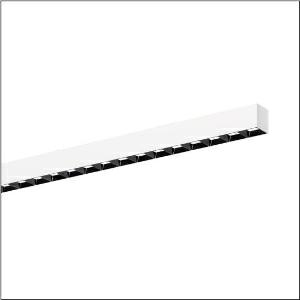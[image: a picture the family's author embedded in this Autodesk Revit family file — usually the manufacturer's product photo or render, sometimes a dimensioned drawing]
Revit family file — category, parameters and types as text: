
# Revit family: silica_r__21_51mx22dc3awb_a852
name_source: partatom
category: Lighting Fixtures
units: mm (PartAtom-declared; Revit-internal decimal feet)

## family parameters
Cut with Voids When Loaded = No
Host = Face
Light Source = No
Part Type = Normal
Room Calculation Point = No
Round Connector Dimension = Use Diameter
Shared = No

## types (1)
- --- (1 x LED, 10800 lm, 69.2 W, 3000K)
    Apparent Load = 69 VA
    CIE Flux Codes = 86 100 100 100 100
    Color Rendering = 80
    Color Temperature = 3000K
    Default Elevation = 1800 mm
    Description = Silica® 21, office luminaire, primary light control with darklight reflector, of PMMA, black, CAT 2 (L<= 3000cd/m²), light emission: direct distribution, primary light characteristic: symmetric, installation type: surface-mounted, LED, rated luminous flux: 10.800lm, luminous efficacy: 156lm/W, light colour: 830, colour temperature: 3000K, with terminal, 3+2-pole, max. 2.5mm², mains connection: 220..240V, AC, 50/60Hz, rated input power: 69.2W, luminaire housing, of aluminium, traffic white (RAL 9016), length: 3.004mm, width: 53mm, height: 53mm, protection rating (complete): IP20, insulation class (complete): insulation class I (protective earthing), certification: CE, permissible operating ambient temperature: 0..+35°C, standard: EN 50419, packaging unit: 1 piece
    Height = 0 mm  [stored 0 ft]
    Lamp = 1 x LED
    Lamp Light Flux = 10800 lm
    Lamp Power = 69.2 W
    Lamp count = 1
    Length = 3004 mm
    Luminous efficacy = 156 lm/W
    Manufacturer = Siteco
    ModVariant = No
    Model = 51MX22DC3AWB
    Mounting Place = Ceiling
    Mounting Type = Recessed
    Number of Poles = 1
    OnlyDefault = Yes
    Power Factor = 1
    Product Name = Silica® 21
    Product group = office luminaire | ceiling recessed
    ProductGroupID = 400
    Protection Class = Protection class I
    Protection Degree = IP 20
    RLX_Detail_Level = 1
    RLX_Emergency_Light_Flux = 0 lm
    RLX_Emergency_Type = 0
    RLX_Emergency_Type_DB = No
    RlxData = <blob elided: 62513 chars, md5=fba1cf44>
    Socket = socket
    Standby Power = 0 W
    System Light Flux = 10800 lm
    System Power = 69 W
    Type Comments = factory setting: luminous flux: 100 % | dim-lin: 254 | 392 mA
    Type Image = l_1335873.jpg
    URL = http://relux.com
    VarID = @adj_095099
    Voltage = 0 V
    Weight = 0.00 kg
    Width = 53 mm

note: [stored X ft] marks values corroborated as IEEE doubles in the binary element streams (Revit-internal decimal feet)

## geometry (parser evidence)
native form markers: Blend x4, Sweep x11
no freeform markers — native parametric forms only
